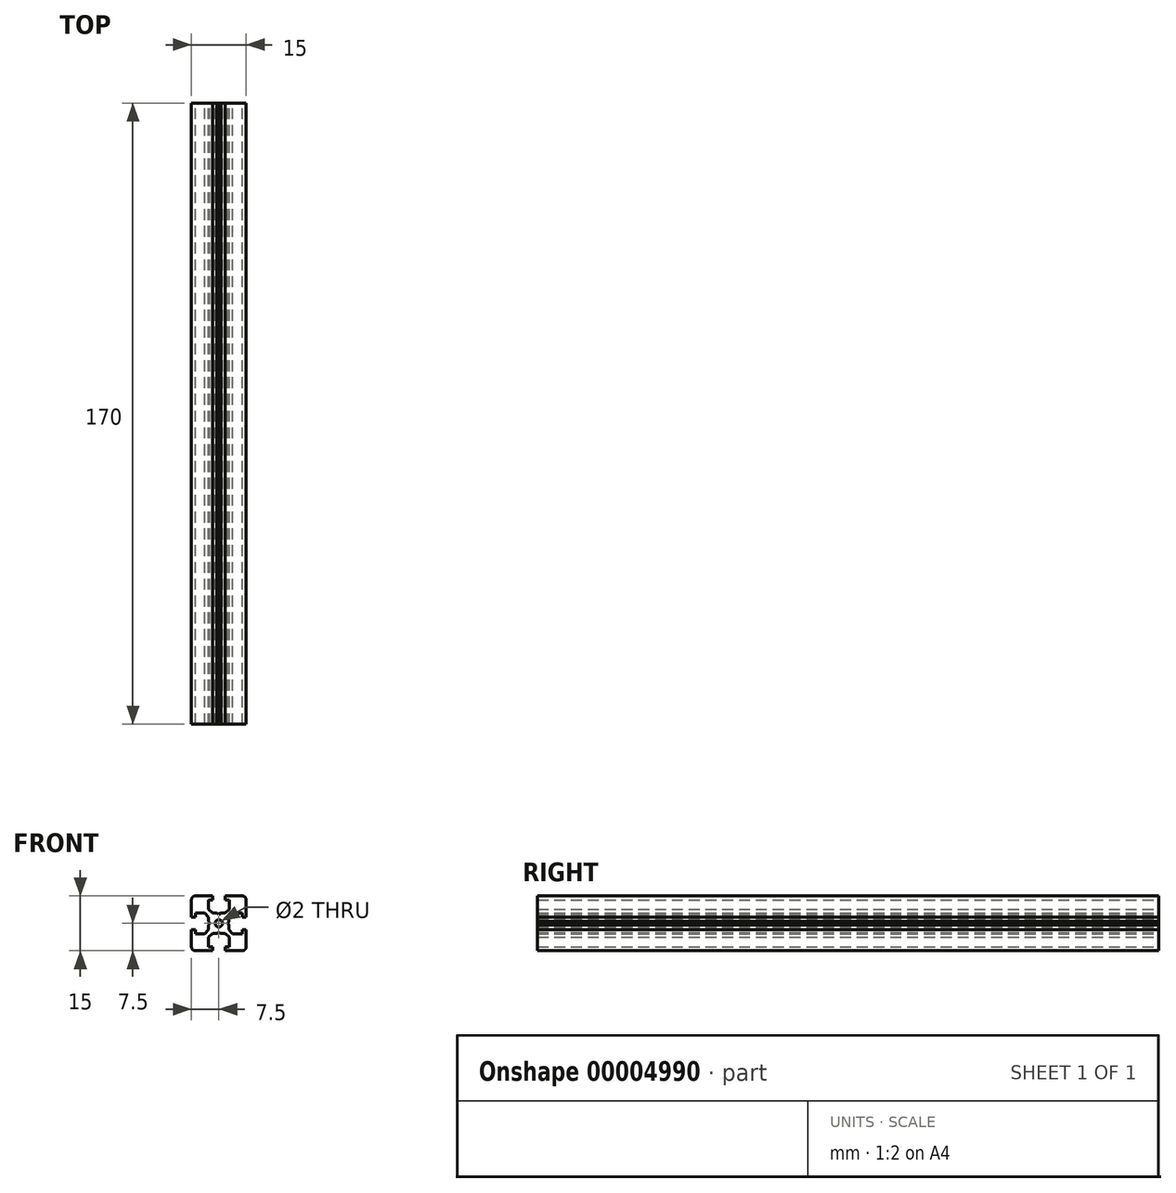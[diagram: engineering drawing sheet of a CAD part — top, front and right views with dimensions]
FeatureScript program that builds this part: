
annotation { "Feature Type Name" : "Feature", "Feature Type Description" : "" }
export const myFeature = defineFeature(function(context is Context, id is Id, definition is map)
    precondition{}
    {
        {
            var Q0;
            Q0=qCreatedBy(makeId("Front.planeOp"),FACE);
            var sketch = newSketch(context, id + "F0", { "sketchPlane" : qUnion([Q0])});
            skCircle(sketch, "E0", {"center": v(0, 0) * mm, "radius": 1 * mm});
            skLineSegment(sketch, "E1.bottom", {"start": v(0, 0) * mm, "end": v(-7.5, 0) * mm, "construction": true});
            skLineSegment(sketch, "E1.top", {"start": v(0, 7.5) * mm, "end": v(-7.5, 7.5) * mm, "construction": true});
            skLineSegment(sketch, "E1.left", {"start": v(0, 0) * mm, "end": v(0, 7.5) * mm, "construction": true});
            skLineSegment(sketch, "E1.right", {"start": v(-7.5, 0) * mm, "end": v(-7.5, 7.5) * mm, "construction": true});
            skLineSegment(sketch, "E2", {"start": v(-2.85, 3.8) * mm, "end": v(-1.7, 2.8) * mm});
            skLineSegment(sketch, "E3", {"start": v(-1.7, 2.8) * mm, "end": v(-0.52, 2.8) * mm});
            skLineSegment(sketch, "E4", {"start": v(-0.52, 2.8) * mm, "end": v(0, 2.5) * mm});
            skLineSegment(sketch, "E5", {"start": v(-7.5, 7.5) * mm, "end": v(-1.7, 7.5) * mm});
            skLineSegment(sketch, "E6", {"start": v(-1.7, 7.5) * mm, "end": v(-1.7, 6.4) * mm});
            skLineSegment(sketch, "E7", {"start": v(-1.7, 6.4) * mm, "end": v(-2.85, 6.4) * mm});
            skLineSegment(sketch, "E8", {"start": v(-2.85, 6.4) * mm, "end": v(-2.85, 3.8) * mm});
            skLineSegment(sketch, "E9", {"start": v(-7.5, 7.5) * mm, "end": v(0, 0) * mm, "construction": true});
            skLineSegment(sketch, "E10.0.MirrorCS", {"start": v(-2.8, 0.52) * mm, "end": v(-2.5, 0) * mm});
            skLineSegment(sketch, "E10.1.MirrorCS", {"start": v(-2.8, 1.7) * mm, "end": v(-2.8, 0.52) * mm});
            skLineSegment(sketch, "E10.2.MirrorCS", {"start": v(-3.8, 2.85) * mm, "end": v(-2.8, 1.7) * mm});
            skLineSegment(sketch, "E10.3.MirrorCS", {"start": v(-6.4, 2.85) * mm, "end": v(-3.8, 2.85) * mm});
            skLineSegment(sketch, "E10.4.MirrorCS", {"start": v(-6.4, 1.7) * mm, "end": v(-6.4, 2.85) * mm});
            skLineSegment(sketch, "E10.5.MirrorCS", {"start": v(-7.5, 1.7) * mm, "end": v(-6.4, 1.7) * mm});
            skLineSegment(sketch, "E10.6.MirrorCS", {"start": v(-7.5, 7.5) * mm, "end": v(-7.5, 1.7) * mm});
            skLineSegment(sketch, "E11.0.MirrorCS", {"start": v(2.8, 0.52) * mm, "end": v(2.5, 0) * mm});
            skLineSegment(sketch, "E11.1.MirrorCS", {"start": v(2.8, 1.7) * mm, "end": v(2.8, 0.52) * mm});
            skLineSegment(sketch, "E11.2.MirrorCS", {"start": v(3.8, 2.85) * mm, "end": v(2.8, 1.7) * mm});
            skLineSegment(sketch, "E11.3.MirrorCS", {"start": v(6.4, 2.85) * mm, "end": v(3.8, 2.85) * mm});
            skLineSegment(sketch, "E11.4.MirrorCS", {"start": v(6.4, 1.7) * mm, "end": v(6.4, 2.85) * mm});
            skLineSegment(sketch, "E11.5.MirrorCS", {"start": v(7.5, 1.7) * mm, "end": v(6.4, 1.7) * mm});
            skLineSegment(sketch, "E11.6.MirrorCS", {"start": v(7.5, 7.5) * mm, "end": v(7.5, 1.7) * mm});
            skLineSegment(sketch, "E11.7.MirrorCS", {"start": v(7.5, 7.5) * mm, "end": v(1.7, 7.5) * mm});
            skLineSegment(sketch, "E11.8.MirrorCS", {"start": v(1.7, 7.5) * mm, "end": v(1.7, 6.4) * mm});
            skLineSegment(sketch, "E11.9.MirrorCS", {"start": v(1.7, 6.4) * mm, "end": v(2.85, 6.4) * mm});
            skLineSegment(sketch, "E11.10.MirrorCS", {"start": v(2.85, 6.4) * mm, "end": v(2.85, 3.8) * mm});
            skLineSegment(sketch, "E11.11.MirrorCS", {"start": v(2.85, 3.8) * mm, "end": v(1.7, 2.8) * mm});
            skLineSegment(sketch, "E11.12.MirrorCS", {"start": v(1.7, 2.8) * mm, "end": v(0.52, 2.8) * mm});
            skLineSegment(sketch, "E11.13.MirrorCS", {"start": v(0.52, 2.8) * mm, "end": v(0, 2.5) * mm});
            skLineSegment(sketch, "E12.0.MirrorCS", {"start": v(2.8, -0.52) * mm, "end": v(2.5, 0) * mm});
            skLineSegment(sketch, "E12.1.MirrorCS", {"start": v(2.8, -1.7) * mm, "end": v(2.8, -0.52) * mm});
            skLineSegment(sketch, "E12.2.MirrorCS", {"start": v(3.8, -2.85) * mm, "end": v(2.8, -1.7) * mm});
            skLineSegment(sketch, "E12.3.MirrorCS", {"start": v(6.4, -2.85) * mm, "end": v(3.8, -2.85) * mm});
            skLineSegment(sketch, "E12.4.MirrorCS", {"start": v(6.4, -1.7) * mm, "end": v(6.4, -2.85) * mm});
            skLineSegment(sketch, "E12.5.MirrorCS", {"start": v(7.5, -1.7) * mm, "end": v(6.4, -1.7) * mm});
            skLineSegment(sketch, "E12.6.MirrorCS", {"start": v(7.5, -7.5) * mm, "end": v(7.5, -1.7) * mm});
            skLineSegment(sketch, "E12.7.MirrorCS", {"start": v(7.5, -7.5) * mm, "end": v(1.7, -7.5) * mm});
            skLineSegment(sketch, "E12.8.MirrorCS", {"start": v(1.7, -7.5) * mm, "end": v(1.7, -6.4) * mm});
            skLineSegment(sketch, "E12.9.MirrorCS", {"start": v(1.7, -6.4) * mm, "end": v(2.85, -6.4) * mm});
            skLineSegment(sketch, "E12.10.MirrorCS", {"start": v(2.85, -6.4) * mm, "end": v(2.85, -3.8) * mm});
            skLineSegment(sketch, "E12.11.MirrorCS", {"start": v(2.85, -3.8) * mm, "end": v(1.7, -2.8) * mm});
            skLineSegment(sketch, "E12.12.MirrorCS", {"start": v(1.7, -2.8) * mm, "end": v(0.52, -2.8) * mm});
            skLineSegment(sketch, "E12.13.MirrorCS", {"start": v(0.52, -2.8) * mm, "end": v(0, -2.5) * mm});
            skLineSegment(sketch, "E12.14.MirrorCS", {"start": v(-0.52, -2.8) * mm, "end": v(0, -2.5) * mm});
            skLineSegment(sketch, "E12.15.MirrorCS", {"start": v(-1.7, -2.8) * mm, "end": v(-0.52, -2.8) * mm});
            skLineSegment(sketch, "E12.16.MirrorCS", {"start": v(-2.85, -3.8) * mm, "end": v(-1.7, -2.8) * mm});
            skLineSegment(sketch, "E12.17.MirrorCS", {"start": v(-2.85, -6.4) * mm, "end": v(-2.85, -3.8) * mm});
            skLineSegment(sketch, "E12.18.MirrorCS", {"start": v(-1.7, -6.4) * mm, "end": v(-2.85, -6.4) * mm});
            skLineSegment(sketch, "E12.19.MirrorCS", {"start": v(-1.7, -7.5) * mm, "end": v(-1.7, -6.4) * mm});
            skLineSegment(sketch, "E12.20.MirrorCS", {"start": v(-7.5, -7.5) * mm, "end": v(-1.7, -7.5) * mm});
            skLineSegment(sketch, "E12.21.MirrorCS", {"start": v(-7.5, -7.5) * mm, "end": v(-7.5, -1.7) * mm});
            skLineSegment(sketch, "E12.22.MirrorCS", {"start": v(-7.5, -1.7) * mm, "end": v(-6.4, -1.7) * mm});
            skLineSegment(sketch, "E12.23.MirrorCS", {"start": v(-6.4, -1.7) * mm, "end": v(-6.4, -2.85) * mm});
            skLineSegment(sketch, "E12.24.MirrorCS", {"start": v(-6.4, -2.85) * mm, "end": v(-3.8, -2.85) * mm});
            skLineSegment(sketch, "E12.25.MirrorCS", {"start": v(-3.8, -2.85) * mm, "end": v(-2.8, -1.7) * mm});
            skLineSegment(sketch, "E12.26.MirrorCS", {"start": v(-2.8, -1.7) * mm, "end": v(-2.8, -0.52) * mm});
            skLineSegment(sketch, "E12.27.MirrorCS", {"start": v(-2.8, -0.52) * mm, "end": v(-2.5, 0) * mm});
            skSolve(sketch);
        }
        {
            var Q0;
            Q0=qSketchRegion(id+"F0",true);
            extrude(context, id + "F1", {"entities" : qUnion([Q0]), "depth" : 170 * mm, "symmetric" : true});
        }
        {
            var Q0;
            Q0=makeQuery(id+"F1.opExtrude","SWEPT_EDGE",EDGE,{"disambiguationData":[OSD([sQuery(id+"F0.wireOp",EDGE,"E11.6.MirrorCS"),sQuery(id+"F0.wireOp",EDGE,"E11.7.MirrorCS")])]});
            var Q1;
            Q1=makeQuery(id+"F1.opExtrude","SWEPT_EDGE",EDGE,{"disambiguationData":[OSD([sQuery(id+"F0.wireOp",EDGE,"E5"),sQuery(id+"F0.wireOp",EDGE,"E10.6.MirrorCS")])]});
            var Q2;
            Q2=makeQuery(id+"F1.opExtrude","SWEPT_EDGE",EDGE,{"disambiguationData":[OSD([sQuery(id+"F0.wireOp",EDGE,"E12.6.MirrorCS"),sQuery(id+"F0.wireOp",EDGE,"E12.7.MirrorCS")])]});
            var Q3;
            Q3=makeQuery(id+"F1.opExtrude","SWEPT_EDGE",EDGE,{"disambiguationData":[OSD([sQuery(id+"F0.wireOp",EDGE,"E12.20.MirrorCS"),sQuery(id+"F0.wireOp",EDGE,"E12.21.MirrorCS")])]});
            fillet(context, id + "F2", {"entities" : qUnion([Q0, Q1, Q2, Q3]), "radius" : 1.1 * mm, "tangentPropagation" : true, "allowEdgeOverflow" : false});
        }
    });
